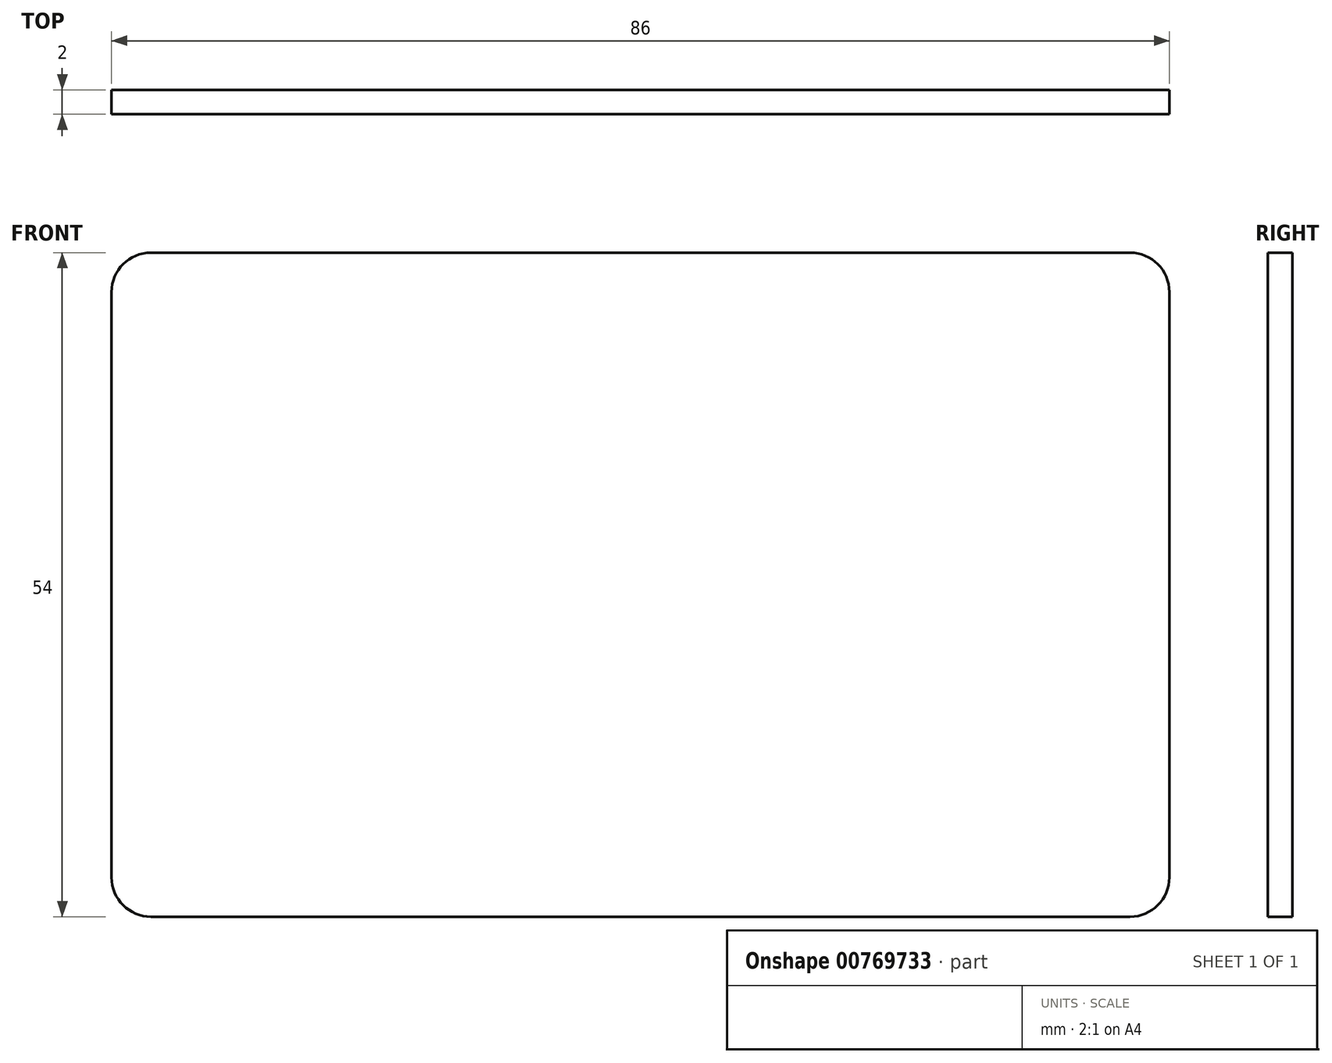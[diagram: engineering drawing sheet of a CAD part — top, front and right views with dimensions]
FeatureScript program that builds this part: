
annotation { "Feature Type Name" : "Feature", "Feature Type Description" : "" }
export const myFeature = defineFeature(function(context is Context, id is Id, definition is map)
    precondition{}
    {
        {
            var Q0;
            Q0=qCreatedBy(makeId("Front.planeOp"),FACE);
            var sketch = newSketch(context, id + "F0", { "sketchPlane" : qUnion([Q0])});
            skLineSegment(sketch, "E0.bottom", {"start": v(3.2, 0) * mm, "end": v(82.8, 0) * mm});
            skLineSegment(sketch, "E0.top", {"start": v(3.2, 54) * mm, "end": v(82.8, 54) * mm});
            skLineSegment(sketch, "E0.left", {"start": v(0, 3.2) * mm, "end": v(0, 50.8) * mm});
            skLineSegment(sketch, "E0.right", {"start": v(86, 3.2) * mm, "end": v(86, 50.8) * mm});
            skLineSegment(sketch, "E1", {"start": v(43, 54) * mm, "end": v(43, 0) * mm, "construction": true});
            skLineSegment(sketch, "E2", {"start": v(0, 27) * mm, "end": v(86, 27) * mm, "construction": true});
            skPoint(sketch, "E3.visualSharp", {"position": v(0, 54) * mm});
            skArc(sketch, "E3.filletArc", {"start": v(3.2, 54) * mm, "mid": v(0.94, 53.06) * mm, "end": v(0, 50.8) * mm});
            skPoint(sketch, "E4.visualSharp", {"position": v(0, 0) * mm});
            skArc(sketch, "E4.filletArc", {"start": v(0, 3.2) * mm, "mid": v(0.94, 0.94) * mm, "end": v(3.2, 0) * mm});
            skPoint(sketch, "E5.visualSharp", {"position": v(86, 54) * mm});
            skArc(sketch, "E5.filletArc", {"start": v(86, 50.8) * mm, "mid": v(85.06, 53.06) * mm, "end": v(82.8, 54) * mm});
            skPoint(sketch, "E6.visualSharp", {"position": v(86, 0) * mm});
            skArc(sketch, "E6.filletArc", {"start": v(82.8, 0) * mm, "mid": v(85.06, 0.94) * mm, "end": v(86, 3.2) * mm});
            skSolve(sketch);
        }
        {
            var Q0;
            Q0 = qSketchRegion(id + "F0", true);
            extrude(context, id + "F1", {"entities" : qUnion([Q0]), "depth" : 2 * mm, "offsetDistance" : 25 * mm});
        }
    });
